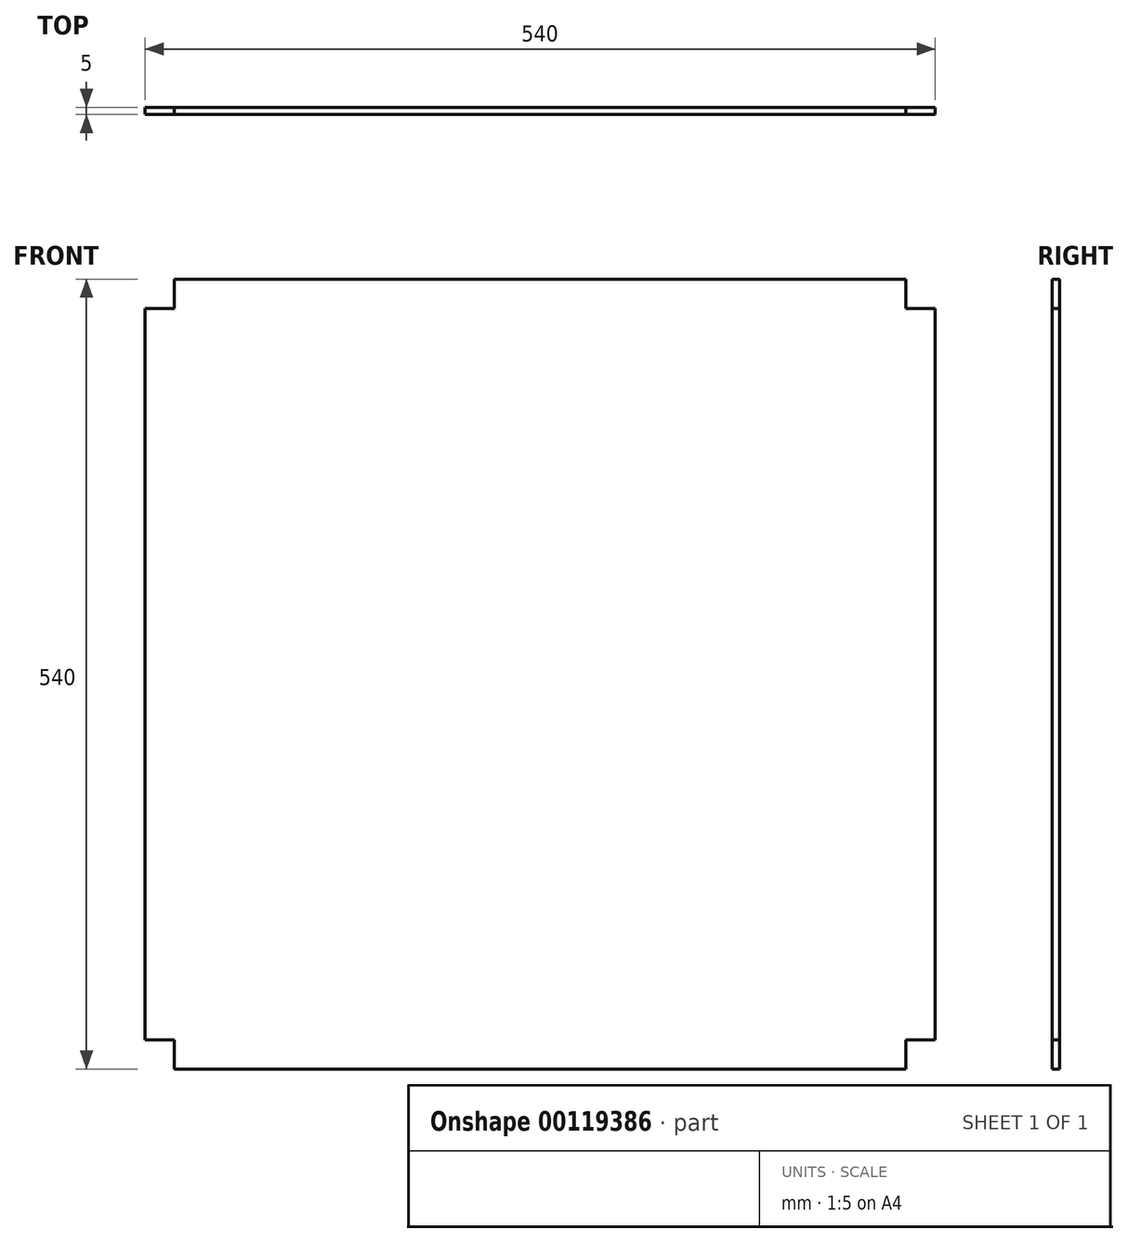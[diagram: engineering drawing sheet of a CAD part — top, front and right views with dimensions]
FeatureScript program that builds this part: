
annotation { "Feature Type Name" : "Feature", "Feature Type Description" : "" }
export const myFeature = defineFeature(function(context is Context, id is Id, definition is map)
    precondition{}
    {
        {
            var Q0;
            Q0=qCreatedBy(makeId("Front.planeOp"),FACE);
            var sketch = newSketch(context, id + "F0", { "sketchPlane" : qUnion([Q0])});
            skLineSegment(sketch, "E0.bottom", {"start": v(250, -270) * mm, "end": v(-250, -270) * mm});
            skLineSegment(sketch, "E0.top", {"start": v(250, 270) * mm, "end": v(-250, 270) * mm});
            skLineSegment(sketch, "E0.left", {"start": v(270, -250) * mm, "end": v(270, 250) * mm});
            skLineSegment(sketch, "E0.right", {"start": v(-270, -250) * mm, "end": v(-270, 250) * mm});
            skPoint(sketch, "E0.middle", {"position": v(0, 0) * mm});
            skLineSegment(sketch, "E1.top", {"start": v(-270, 250) * mm, "end": v(-250, 250) * mm});
            skLineSegment(sketch, "E1.right", {"start": v(-250, 270) * mm, "end": v(-250, 250) * mm});
            skLineSegment(sketch, "E2.0.1.1", {"start": v(-270, -250) * mm, "end": v(-250, -250) * mm});
            skLineSegment(sketch, "E2.0.1.3", {"start": v(-250, -250) * mm, "end": v(-250, -270) * mm});
            skLineSegment(sketch, "E2.1.0.0", {"start": v(250, 250) * mm, "end": v(270, 250) * mm});
            skLineSegment(sketch, "E2.1.0.2", {"start": v(250, 270) * mm, "end": v(250, 250) * mm});
            skLineSegment(sketch, "E2.1.1.1", {"start": v(250, -250) * mm, "end": v(270, -250) * mm});
            skLineSegment(sketch, "E2.1.1.2", {"start": v(250, -250) * mm, "end": v(250, -270) * mm});
            skLineSegment(sketch, "E2.direction1", {"start": v(-270, 250) * mm, "end": v(250, 250) * mm, "construction": true});
            skLineSegment(sketch, "E2.direction2", {"start": v(-270, 250) * mm, "end": v(-270, -250) * mm, "construction": true});
            skPoint(sketch, "E3.orphan", {"position": v(-270, 270) * mm});
            skPoint(sketch, "E4.orphan", {"position": v(270, 270) * mm});
            skPoint(sketch, "E5.orphan", {"position": v(270, -270) * mm});
            skPoint(sketch, "E6.orphan", {"position": v(-270, -270) * mm});
            skSolve(sketch);
        }
        {
            var Q0;
            Q0=makeQuery(id+"F0.imprint","IMPRINT",FACE,{"disambiguationData":[TD([[makeQuery(id+"F0.imprint","IMPRINT",EDGE,{"derivedFrom":sQuery(id+"F0.wireOp",EDGE,"E0.bottom")}),-1.0]])]});
            extrude(context, id + "F1", {"entities" : qUnion([Q0]), "depth" : 5 * mm});
        }
    });
